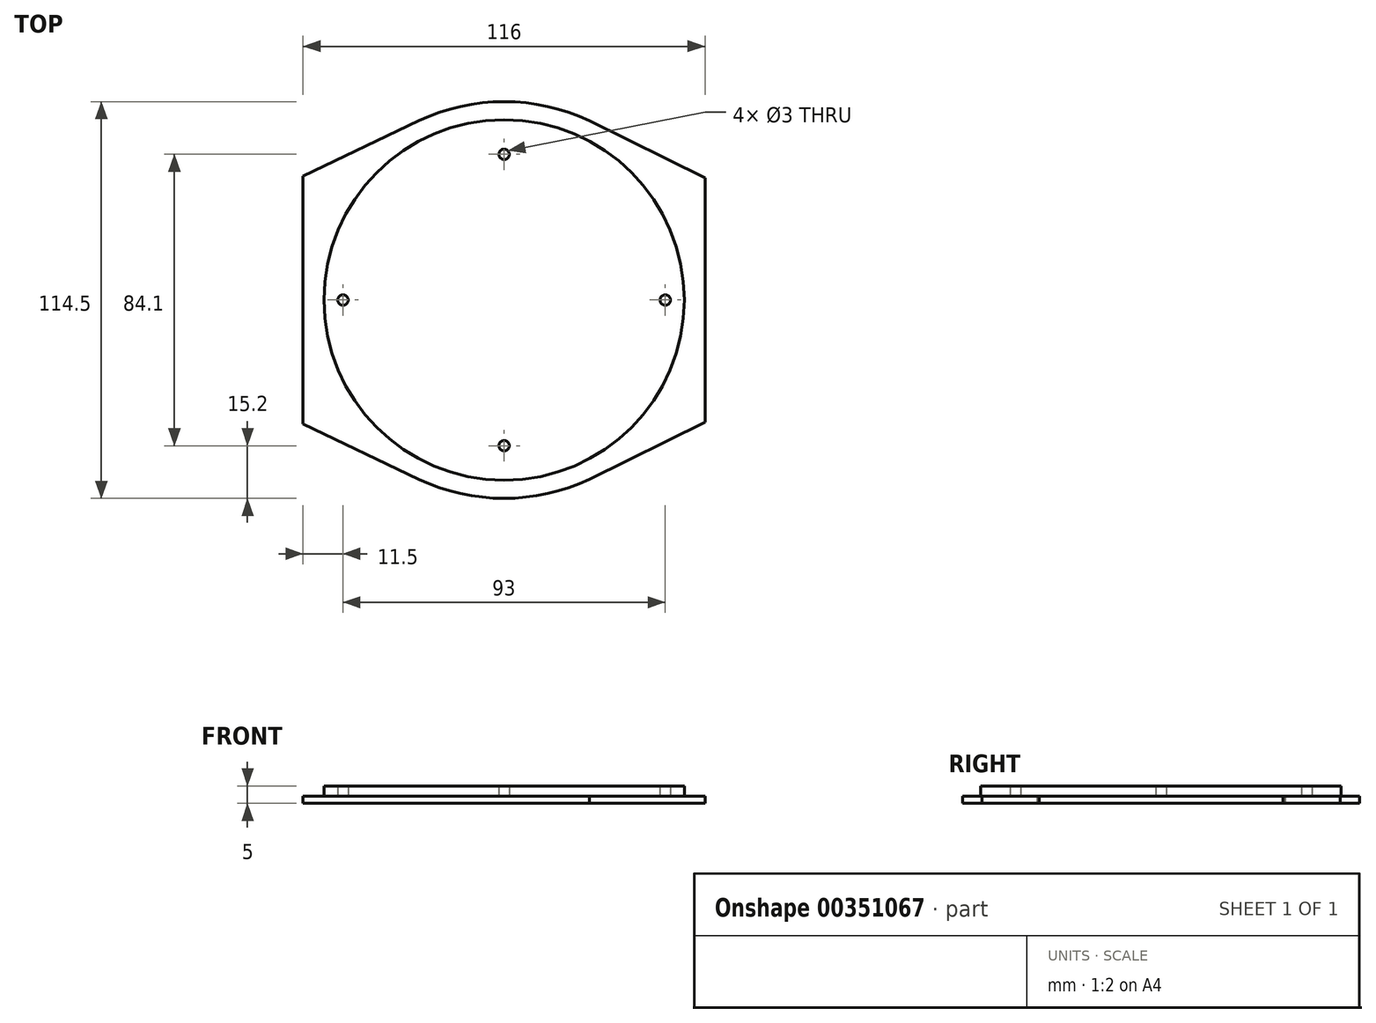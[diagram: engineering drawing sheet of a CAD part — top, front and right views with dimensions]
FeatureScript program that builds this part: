
annotation { "Feature Type Name" : "Feature", "Feature Type Description" : "" }
export const myFeature = defineFeature(function(context is Context, id is Id, definition is map)
    precondition{}
    {
        {
            var Q0;
            Q0=qCreatedBy(makeId("Top.planeOp"),FACE);
            var sketch = newSketch(context, id + "F0", { "sketchPlane" : qUnion([Q0])});
            skCircle(sketch, "E0", {"center": v(0, 0) * mm, "radius": 52 * mm});
            skCircle(sketch, "E1", {"center": v(46.5, 0) * mm, "radius": 1.5 * mm});
            skCircle(sketch, "E2", {"center": v(0, -42.05) * mm, "radius": 1.5 * mm});
            skCircle(sketch, "E3.MirrorC", {"center": v(-46.5, 0) * mm, "radius": 1.5 * mm});
            skCircle(sketch, "E4.MirrorC", {"center": v(0, 42.05) * mm, "radius": 1.5 * mm});
            skSolve(sketch);
        }
        {
            var Q0;
            Q0=makeQuery(id+"F0.imprint","IMPRINT",FACE,{"disambiguationData":[TD([[makeQuery(id+"F0.imprint","IMPRINT",EDGE,{"derivedFrom":sQuery(id+"F0.wireOp",EDGE,"E0")}),1.0]])]});
            var Q1;
            Q1=makeQuery(id+"F0.imprint","IMPRINT",FACE,{"disambiguationData":[TD([[makeQuery(id+"F0.imprint","IMPRINT",EDGE,{"derivedFrom":sQuery(id+"F0.wireOp",EDGE,"E0")}),-1.0]])]});
            extrude(context, id + "F1", {"entities" : qUnion([Q0, Q1]), "depth" : 5 * mm});
        }
        {
            var Q0;
            Q0=qCreatedBy(makeId("Top.planeOp"),FACE);
            var sketch = newSketch(context, id + "F2", { "sketchPlane" : qUnion([Q0])});
            skLineSegment(sketch, "E5", {"start": v(-58, 35.8) * mm, "end": v(-24.6, 51.7) * mm});
            skArc(sketch, "E6", {"start": v(24.6, 51.7) * mm, "mid": v(0, 57.25) * mm, "end": v(-24.6, 51.7) * mm});
            skLineSegment(sketch, "E7", {"start": v(24.6, 51.7) * mm, "end": v(58, 35.22) * mm});
            skLineSegment(sketch, "E8", {"start": v(58, 35.22) * mm, "end": v(58, 0) * mm});
            skLineSegment(sketch, "E9", {"start": v(-58, 35.8) * mm, "end": v(-58, 0) * mm});
            skLineSegment(sketch, "E10.MirrorCS", {"start": v(-58, -35.8) * mm, "end": v(-58, 0) * mm});
            skLineSegment(sketch, "E11.MirrorCS", {"start": v(-58, -35.8) * mm, "end": v(-24.6, -51.7) * mm});
            skArc(sketch, "E12.MirrorCS", {"start": v(24.6, -51.7) * mm, "mid": v(0, -57.25) * mm, "end": v(-24.6, -51.7) * mm});
            skLineSegment(sketch, "E13.MirrorCS", {"start": v(24.6, -51.7) * mm, "end": v(58, -35.22) * mm});
            skLineSegment(sketch, "E14.MirrorCS", {"start": v(58, -35.22) * mm, "end": v(58, 0) * mm});
            skSolve(sketch);
        }
        {
            var Q0;
            Q0=makeQuery(id+"F2.imprint","IMPRINT",FACE,{"disambiguationData":[TD([[makeQuery(id+"F2.imprint","IMPRINT",EDGE,{"derivedFrom":sQuery(id+"F2.wireOp",EDGE,"E5")}),-1.0]])]});
            extrude(context, id + "F3", {"entities" : qUnion([Q0]), "operationType" : NewBodyOperationType.ADD, "depth" : 2 * mm});
        }
        {
            var Q0;
            Q0=makeQuery(id+"F3.boolean.opBoolean","SPLIT",FACE,{"disambiguationData":[TD([makeQuery(id+"F1.opExtrude","SWEPT_FACE",FACE,{"disambiguationData":[OSD([sQuery(id+"F0.wireOp",EDGE,"E4.MirrorC")])]})])],"derivedFrom":makeQuery(id+"F3.opExtrude","CAP_FACE",FACE,{"disambiguationData":[OSD([sQuery(id+"F2.wireOp",EDGE,"E5"),sQuery(id+"F2.wireOp",EDGE,"E6"),sQuery(id+"F2.wireOp",EDGE,"E7"),sQuery(id+"F2.wireOp",EDGE,"E8"),sQuery(id+"F2.wireOp",EDGE,"E9"),sQuery(id+"F2.wireOp",EDGE,"E10.MirrorCS"),sQuery(id+"F2.wireOp",EDGE,"E11.MirrorCS"),sQuery(id+"F2.wireOp",EDGE,"E12.MirrorCS"),sQuery(id+"F2.wireOp",EDGE,"E13.MirrorCS"),sQuery(id+"F2.wireOp",EDGE,"E14.MirrorCS")])],"isStart":false})});
            var Q1;
            Q1=makeQuery(id+"F3.boolean.opBoolean","SPLIT",FACE,{"disambiguationData":[TD([makeQuery(id+"F1.opExtrude","SWEPT_FACE",FACE,{"disambiguationData":[OSD([sQuery(id+"F0.wireOp",EDGE,"E1")])]})])],"derivedFrom":makeQuery(id+"F3.opExtrude","CAP_FACE",FACE,{"disambiguationData":[OSD([sQuery(id+"F2.wireOp",EDGE,"E5"),sQuery(id+"F2.wireOp",EDGE,"E6"),sQuery(id+"F2.wireOp",EDGE,"E7"),sQuery(id+"F2.wireOp",EDGE,"E8"),sQuery(id+"F2.wireOp",EDGE,"E9"),sQuery(id+"F2.wireOp",EDGE,"E10.MirrorCS"),sQuery(id+"F2.wireOp",EDGE,"E11.MirrorCS"),sQuery(id+"F2.wireOp",EDGE,"E12.MirrorCS"),sQuery(id+"F2.wireOp",EDGE,"E13.MirrorCS"),sQuery(id+"F2.wireOp",EDGE,"E14.MirrorCS")])],"isStart":false})});
            var Q2;
            Q2=makeQuery(id+"F3.boolean.opBoolean","SPLIT",FACE,{"disambiguationData":[TD([makeQuery(id+"F1.opExtrude","SWEPT_FACE",FACE,{"disambiguationData":[OSD([sQuery(id+"F0.wireOp",EDGE,"E2")])]})])],"derivedFrom":makeQuery(id+"F3.opExtrude","CAP_FACE",FACE,{"disambiguationData":[OSD([sQuery(id+"F2.wireOp",EDGE,"E5"),sQuery(id+"F2.wireOp",EDGE,"E6"),sQuery(id+"F2.wireOp",EDGE,"E7"),sQuery(id+"F2.wireOp",EDGE,"E8"),sQuery(id+"F2.wireOp",EDGE,"E9"),sQuery(id+"F2.wireOp",EDGE,"E10.MirrorCS"),sQuery(id+"F2.wireOp",EDGE,"E11.MirrorCS"),sQuery(id+"F2.wireOp",EDGE,"E12.MirrorCS"),sQuery(id+"F2.wireOp",EDGE,"E13.MirrorCS"),sQuery(id+"F2.wireOp",EDGE,"E14.MirrorCS")])],"isStart":false})});
            var Q3;
            Q3=makeQuery(id+"F3.boolean.opBoolean","SPLIT",FACE,{"disambiguationData":[TD([makeQuery(id+"F1.opExtrude","SWEPT_FACE",FACE,{"disambiguationData":[OSD([sQuery(id+"F0.wireOp",EDGE,"E3.MirrorC")])]})])],"derivedFrom":makeQuery(id+"F3.opExtrude","CAP_FACE",FACE,{"disambiguationData":[OSD([sQuery(id+"F2.wireOp",EDGE,"E5"),sQuery(id+"F2.wireOp",EDGE,"E6"),sQuery(id+"F2.wireOp",EDGE,"E7"),sQuery(id+"F2.wireOp",EDGE,"E8"),sQuery(id+"F2.wireOp",EDGE,"E9"),sQuery(id+"F2.wireOp",EDGE,"E10.MirrorCS"),sQuery(id+"F2.wireOp",EDGE,"E11.MirrorCS"),sQuery(id+"F2.wireOp",EDGE,"E12.MirrorCS"),sQuery(id+"F2.wireOp",EDGE,"E13.MirrorCS"),sQuery(id+"F2.wireOp",EDGE,"E14.MirrorCS")])],"isStart":false})});
            extrude(context, id + "F4", {"entities" : qUnion([Q0, Q1, Q2, Q3]), "operationType" : NewBodyOperationType.REMOVE, "endBound" : BoundingType.THROUGH_ALL, "oppositeDirection" : true, "depth" : 25 * mm});
        }
    });
